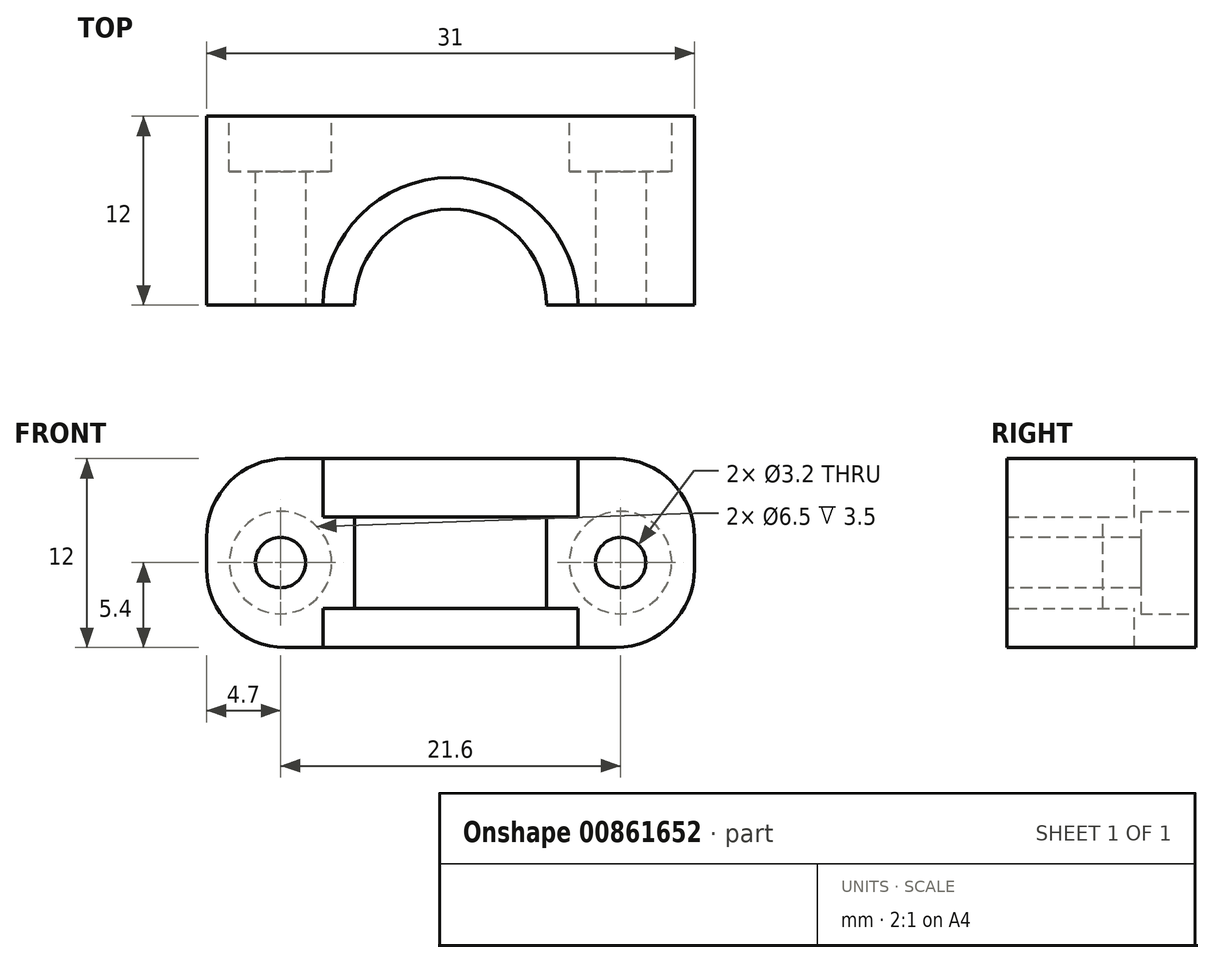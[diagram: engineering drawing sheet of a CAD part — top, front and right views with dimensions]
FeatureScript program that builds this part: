
annotation { "Feature Type Name" : "Feature", "Feature Type Description" : "" }
export const myFeature = defineFeature(function(context is Context, id is Id, definition is map)
    precondition{}
    {
        {
            var Q0;
            Q0=qCreatedBy(makeId("Top.planeOp"),FACE);
            var sketch = newSketch(context, id + "F0", { "sketchPlane" : qUnion([Q0])});
            skCircle(sketch, "E0", {"center": v(0, 0) * mm, "radius": 6 * mm, "construction": true});
            skArc(sketch, "E1", {"start": v(8, 0) * mm, "mid": v(0, 8) * mm, "end": v(-8, 0) * mm, "construction": true});
            skLineSegment(sketch, "E2", {"start": v(0, 0) * mm, "end": v(0, 28.41) * mm, "construction": true});
            skLineSegment(sketch, "E3.bottom", {"start": v(-14, 0) * mm, "end": v(-8, 0) * mm, "construction": true});
            skLineSegment(sketch, "E3.top", {"start": v(-14, 3.8) * mm, "end": v(-8, 3.8) * mm, "construction": true});
            skLineSegment(sketch, "E3.left", {"start": v(-14, 0) * mm, "end": v(-14, 3.8) * mm, "construction": true});
            skLineSegment(sketch, "E3.right", {"start": v(-8, 0) * mm, "end": v(-8, 3.8) * mm, "construction": true});
            skLineSegment(sketch, "E4.MirrorCS", {"start": v(14, 3.8) * mm, "end": v(8, 3.8) * mm, "construction": true});
            skLineSegment(sketch, "E5.MirrorCS", {"start": v(14, 0) * mm, "end": v(14, 3.8) * mm, "construction": true});
            skLineSegment(sketch, "E6.MirrorCS", {"start": v(14, 0) * mm, "end": v(8, 0) * mm, "construction": true});
            skLineSegment(sketch, "E7.MirrorCS", {"start": v(8, 0) * mm, "end": v(8, 3.8) * mm, "construction": true});
            skLineSegment(sketch, "E8", {"start": v(-15.5, 12) * mm, "end": v(-15.5, 0) * mm});
            skLineSegment(sketch, "E9", {"start": v(-15.5, 0) * mm, "end": v(-8, 0) * mm});
            skLineSegment(sketch, "E10", {"start": v(8, 0) * mm, "end": v(15.5, 0) * mm});
            skLineSegment(sketch, "E11", {"start": v(15.5, 0) * mm, "end": v(15.5, 12) * mm});
            skLineSegment(sketch, "E12", {"start": v(15.5, 12) * mm, "end": v(-15.5, 12) * mm});
            skArc(sketch, "E13", {"start": v(8.1, 0) * mm, "mid": v(0, 8.1) * mm, "end": v(-8.1, 0) * mm});
            skSolve(sketch);
        }
        {
            var Q0;
            Q0 = qSketchRegion(id + "F0", true);
            extrude(context, id + "F1", {"entities" : qUnion([Q0]), "oppositeDirection" : true, "depth" : 3.7 * mm, "offsetDistance" : 25 * mm});
        }
        {
            var Q0;
            Q0=makeQuery(id+"F1.opExtrude","CAP_FACE",FACE,{"disambiguationData":[OSD([sQuery(id+"F0.wireOp",EDGE,"E8"),sQuery(id+"F0.wireOp",EDGE,"E9"),sQuery(id+"F0.wireOp",EDGE,"E10"),sQuery(id+"F0.wireOp",EDGE,"E11"),sQuery(id+"F0.wireOp",EDGE,"E12"),sQuery(id+"F0.wireOp",EDGE,"E13")])],"isStart":false});
            var sketch = newSketch(context, id + "F2", { "sketchPlane" : qUnion([Q0])});
            skLineSegment(sketch, "E14.0.0", {"start": v(15.5, -12) * mm, "end": v(15.5, 0) * mm});
            skLineSegment(sketch, "E14.0.1", {"start": v(15.5, 0) * mm, "end": v(6.1, 0) * mm});
            skLineSegment(sketch, "E14.0.3", {"start": v(-8.1, 0) * mm, "end": v(-15.5, 0) * mm});
            skLineSegment(sketch, "E14.0.4", {"start": v(-15.5, 0) * mm, "end": v(-15.5, -12) * mm});
            skLineSegment(sketch, "E14.0.5", {"start": v(-15.5, -12) * mm, "end": v(0, -12) * mm});
            skLineSegment(sketch, "E14.0.6", {"start": v(0, -12) * mm, "end": v(15.5, -12) * mm});
            skArc(sketch, "E15", {"start": v(-6.1, 0) * mm, "mid": v(0, -6.1) * mm, "end": v(6.1, 0) * mm});
            skLineSegment(sketch, "E16", {"start": v(-8.1, 0) * mm, "end": v(-6.1, 0) * mm});
            skLineSegment(sketch, "E17.trimOffspring", {"start": v(-15.5, 0) * mm, "end": v(-6.1, 0) * mm});
            skLineSegment(sketch, "E18.trimOffspring", {"start": v(-6.1, 0) * mm, "end": v(-15.5, 0) * mm});
            skSolve(sketch);
        }
        {
            var Q0;
            Q0 = qSketchRegion(id + "F2", true);
            extrude(context, id + "F3", {"entities" : qUnion([Q0]), "operationType" : NewBodyOperationType.ADD, "depth" : 5.8 * mm, "offsetDistance" : 25 * mm});
        }
        {
            var Q0;
            Q0=makeQuery(id+"F3.opExtrude","CAP_FACE",FACE,{"disambiguationData":[OSD([sQuery(id+"F2.wireOp",EDGE,"E14.0.0"),sQuery(id+"F2.wireOp",EDGE,"E14.0.1"),sQuery(id+"F2.wireOp",EDGE,"E14.0.4"),sQuery(id+"F2.wireOp",EDGE,"E14.0.5"),sQuery(id+"F2.wireOp",EDGE,"E14.0.6"),sQuery(id+"F2.wireOp",EDGE,"E15"),sQuery(id+"F2.wireOp",EDGE,"E18.trimOffspring")])],"isStart":false});
            var sketch = newSketch(context, id + "F4", { "sketchPlane" : qUnion([Q0])});
            skLineSegment(sketch, "E19.0.0", {"start": v(8.1, 0) * mm, "end": v(15.5, 0) * mm});
            skLineSegment(sketch, "E19.0.1", {"start": v(15.5, 0) * mm, "end": v(15.5, -12) * mm});
            skLineSegment(sketch, "E19.0.2", {"start": v(15.5, -12) * mm, "end": v(-15.5, -12) * mm});
            skLineSegment(sketch, "E19.0.3", {"start": v(-15.5, -12) * mm, "end": v(-15.5, 0) * mm});
            skLineSegment(sketch, "E19.0.4", {"start": v(-15.5, 0) * mm, "end": v(-8.1, 0) * mm});
            skArc(sketch, "E19.0.5", {"start": v(-8.1, 0) * mm, "mid": v(0, -8.1) * mm, "end": v(8.1, 0) * mm});
            skSolve(sketch);
        }
        {
            var Q0;
            Q0 = qSketchRegion(id + "F4", true);
            extrude(context, id + "F5", {"entities" : qUnion([Q0]), "operationType" : NewBodyOperationType.ADD, "depth" : 2.5 * mm, "offsetDistance" : 25 * mm});
        }
        {
            var Q0;
            Q0=makeQuery(id+"F5.boolean.opBoolean","MERGE",FACE,{"derivedFrom":[makeQuery(id+"F3.boolean.opBoolean","MERGE",FACE,{"derivedFrom":[makeQuery(id+"F1.opExtrude","SWEPT_FACE",FACE,{"disambiguationData":[OSD([sQuery(id+"F0.wireOp",EDGE,"E9")])]}),makeQuery(id+"F3.opExtrude","SWEPT_FACE",FACE,{"disambiguationData":[OSD([sQuery(id+"F2.wireOp",EDGE,"E18.trimOffspring")])]})]}),makeQuery(id+"F5.opExtrude","SWEPT_FACE",FACE,{"disambiguationData":[OSD([sQuery(id+"F4.wireOp",EDGE,"E19.0.4")])]})]});
            var sketch = newSketch(context, id + "F6", { "sketchPlane" : qUnion([Q0])});
            skLineSegment(sketch, "E20", {"start": v(-6.1, -6.6) * mm, "end": v(-10.8, -6.6) * mm, "construction": true});
            skCircle(sketch, "E21", {"center": v(-10.8, -6.6) * mm, "radius": 1.6 * mm});
            skLineSegment(sketch, "E22.0", {"start": v(6.1, -3.7) * mm, "end": v(-6.1, -3.7) * mm, "construction": true});
            skLineSegment(sketch, "E23", {"start": v(0, -3.7) * mm, "end": v(0, -10.48) * mm, "construction": true});
            skCircle(sketch, "E24.MirrorC", {"center": v(10.8, -6.6) * mm, "radius": 1.6 * mm});
            skSolve(sketch);
        }
        {
            var Q0;
            Q0 = qSketchRegion(id + "F6", true);
            extrude(context, id + "F7", {"entities" : qUnion([Q0]), "operationType" : NewBodyOperationType.REMOVE, "endBound" : BoundingType.THROUGH_ALL, "oppositeDirection" : true, "depth" : 25 * mm, "offsetDistance" : 25 * mm});
        }
        {
            var Q0;
            Q0=makeQuery(id+"F5.boolean.opBoolean","MERGE",FACE,{"derivedFrom":[makeQuery(id+"F3.boolean.opBoolean","MERGE",FACE,{"derivedFrom":[makeQuery(id+"F1.opExtrude","SWEPT_FACE",FACE,{"disambiguationData":[OSD([sQuery(id+"F0.wireOp",EDGE,"E12")])]}),makeQuery(id+"F3.opExtrude","SWEPT_FACE",FACE,{"disambiguationData":[OSD([sQuery(id+"F2.wireOp",EDGE,"E14.0.5"),sQuery(id+"F2.wireOp",EDGE,"E14.0.6")])]})]}),makeQuery(id+"F5.opExtrude","SWEPT_FACE",FACE,{"disambiguationData":[OSD([sQuery(id+"F4.wireOp",EDGE,"E19.0.2")])]})]});
            var sketch = newSketch(context, id + "F8", { "sketchPlane" : qUnion([Q0])});
            skCircle(sketch, "E25", {"center": v(-10.8, -6.6) * mm, "radius": 3.25 * mm});
            skCircle(sketch, "E26", {"center": v(10.8, -6.6) * mm, "radius": 3.25 * mm});
            skSolve(sketch);
        }
        {
            var Q0;
            Q0 = qSketchRegion(id + "F8", true);
            extrude(context, id + "F9", {"entities" : qUnion([Q0]), "operationType" : NewBodyOperationType.REMOVE, "oppositeDirection" : true, "depth" : 3.5 * mm, "offsetDistance" : 25 * mm});
        }
        {
            var Q0;
            Q0=makeQuery(id+"F1.opExtrude","CAP_EDGE",EDGE,{"disambiguationData":[OSD([sQuery(id+"F0.wireOp",EDGE,"E11")])],"isStart":true});
            var Q1;
            Q1=makeQuery(id+"F5.opExtrude","CAP_EDGE",EDGE,{"disambiguationData":[OSD([sQuery(id+"F4.wireOp",EDGE,"E19.0.1")])],"isStart":false});
            var Q2;
            Q2=makeQuery(id+"F1.opExtrude","CAP_EDGE",EDGE,{"disambiguationData":[OSD([sQuery(id+"F0.wireOp",EDGE,"E8")])],"isStart":true});
            var Q3;
            Q3=makeQuery(id+"F5.opExtrude","CAP_EDGE",EDGE,{"disambiguationData":[OSD([sQuery(id+"F4.wireOp",EDGE,"E19.0.3")])],"isStart":false});
            fillet(context, id + "F10", {"entities" : qUnion([Q0, Q1, Q2, Q3]), "radius" : 5 * mm, "tangentPropagation" : true, "allowEdgeOverflow" : false});
        }
    });
